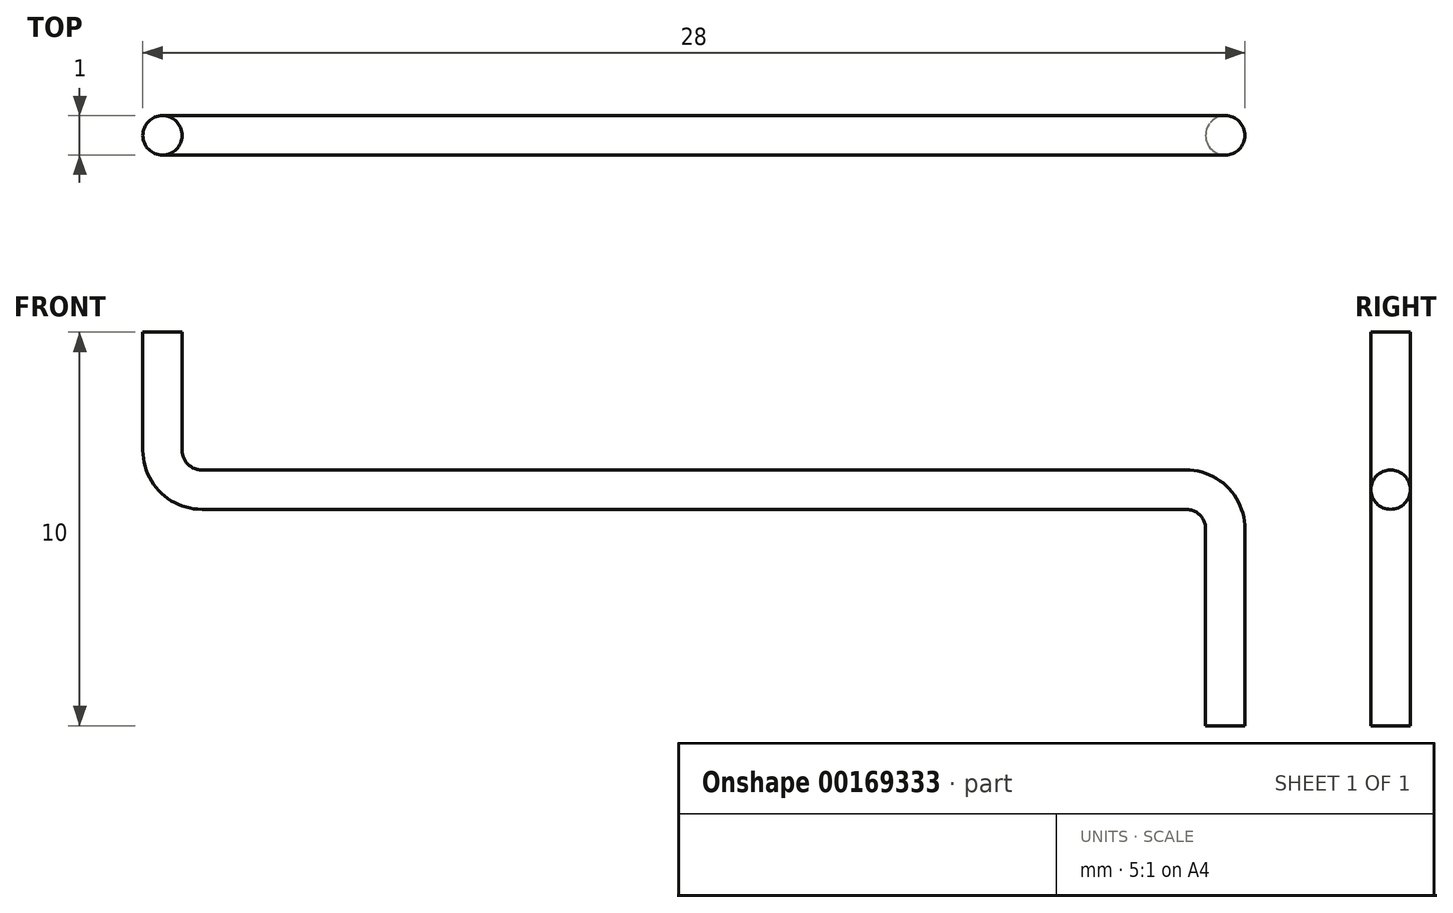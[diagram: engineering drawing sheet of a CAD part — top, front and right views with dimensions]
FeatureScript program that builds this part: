
annotation { "Feature Type Name" : "Feature", "Feature Type Description" : "" }
export const myFeature = defineFeature(function(context is Context, id is Id, definition is map)
    precondition{}
    {
        {
            var Q0;
            Q0=qCreatedBy(makeId("Front.planeOp"),FACE);
            var sketch = newSketch(context, id + "F0", { "sketchPlane" : qUnion([Q0])});
            skLineSegment(sketch, "E0", {"start": v(-13.5, 3) * mm, "end": v(-13.5, 1) * mm});
            skArc(sketch, "E1", {"start": v(-13.5, 1) * mm, "mid": v(-13.2, 0.3) * mm, "end": v(-12.5, 0) * mm});
            skLineSegment(sketch, "E2", {"start": v(-12.5, 0) * mm, "end": v(12.5, 0) * mm});
            skArc(sketch, "E3", {"start": v(12.5, 0) * mm, "mid": v(13.2, -0.3) * mm, "end": v(13.5, -1) * mm});
            skLineSegment(sketch, "E4", {"start": v(13.5, -1) * mm, "end": v(13.5, -6) * mm});
            skLineSegment(sketch, "E5.bottom", {"start": v(-13.5, 3) * mm, "end": v(-13, 3) * mm});
            skLineSegment(sketch, "E5.top", {"start": v(-13.5, 4) * mm, "end": v(-13, 4) * mm});
            skLineSegment(sketch, "E5.left", {"start": v(-13.5, 3) * mm, "end": v(-13.5, 4) * mm});
            skLineSegment(sketch, "E5.right", {"start": v(-13, 3) * mm, "end": v(-13, 4) * mm});
            skSolve(sketch);
        }
        {
            var Q0;
            Q0=makeQuery(id+"F0.imprint","IMPRINT",FACE,{"disambiguationData":[TD([[makeQuery(id+"F0.imprint","IMPRINT",EDGE,{"derivedFrom":sQuery(id+"F0.wireOp",EDGE,"E5.bottom")}),1.0]])]});
            var Q1;
            Q1=sQuery(id+"F0.wireOp",EDGE,"E5.left");
            revolve(context, id + "F1", {"entities" : qUnion([Q0]), "axis" : qUnion([Q1]), "revolveType" : RevolveType.FULL});
        }
        {
            var Q0;
            Q0=makeQuery(id+"F1.opRevolve","SWEPT_FACE",FACE,{"disambiguationData":[OSD([sQuery(id+"F0.wireOp",EDGE,"E5.bottom")])]});
            var Q1;
            Q1=sQuery(id+"F0.wireOp",EDGE,"E0");
            var Q2;
            Q2=sQuery(id+"F0.wireOp",EDGE,"E1");
            var Q3;
            Q3=sQuery(id+"F0.wireOp",EDGE,"E2");
            var Q4;
            Q4=sQuery(id+"F0.wireOp",EDGE,"E3");
            var Q5;
            Q5=sQuery(id+"F0.wireOp",EDGE,"E4");
            sweep(context, id + "F2", {"operationType" : NewBodyOperationType.ADD, "profiles" : qUnion([Q0]), "path" : qUnion([Q1, Q2, Q3, Q4, Q5])});
        }
    });
